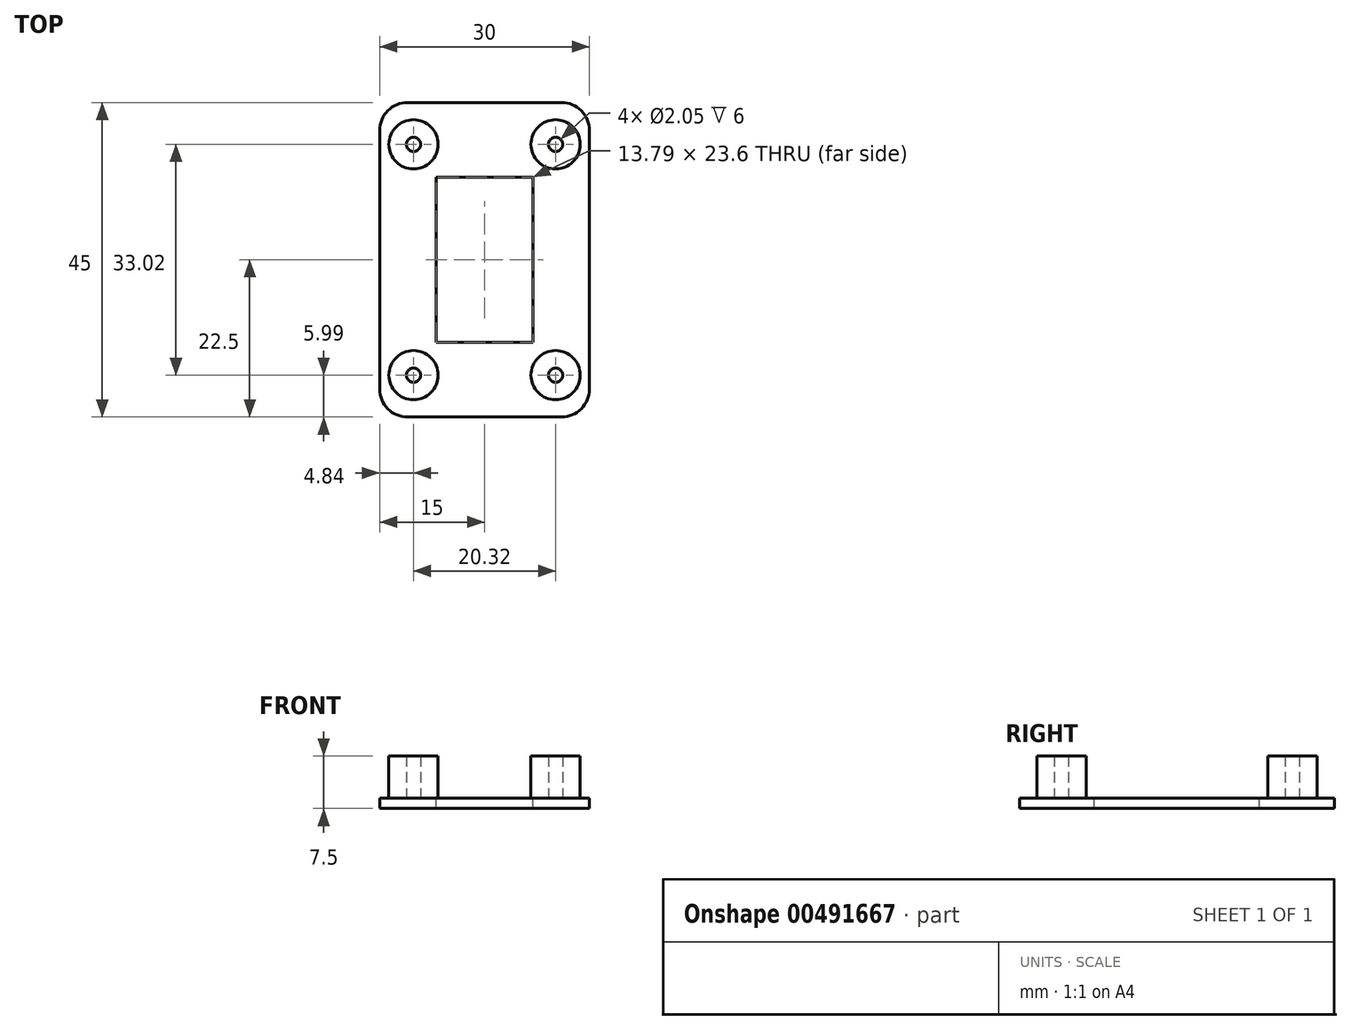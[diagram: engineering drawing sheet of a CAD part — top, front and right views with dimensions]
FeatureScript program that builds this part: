
annotation { "Feature Type Name" : "Feature", "Feature Type Description" : "" }
export const myFeature = defineFeature(function(context is Context, id is Id, definition is map)
    precondition{}
    {
        {
            var Q0;
            Q0=qCreatedBy(makeId("Top.planeOp"),FACE);
            var sketch = newSketch(context, id + "F0", { "sketchPlane" : qUnion([Q0])});
            skLineSegment(sketch, "E0.bottom", {"start": v(-11, 22.5) * mm, "end": v(11, 22.5) * mm});
            skLineSegment(sketch, "E0.top", {"start": v(-11, -22.5) * mm, "end": v(11, -22.5) * mm});
            skLineSegment(sketch, "E0.left", {"start": v(-15, 18.5) * mm, "end": v(-15, -18.5) * mm});
            skLineSegment(sketch, "E0.right", {"start": v(15, 18.5) * mm, "end": v(15, -18.5) * mm});
            skPoint(sketch, "E0.middle", {"position": v(0, 0) * mm});
            skPoint(sketch, "E1.visualSharp", {"position": v(-15, -22.5) * mm});
            skArc(sketch, "E1.filletArc", {"start": v(-15, -18.5) * mm, "mid": v(-13.83, -21.33) * mm, "end": v(-11, -22.5) * mm});
            skPoint(sketch, "E2.visualSharp", {"position": v(15, -22.5) * mm});
            skArc(sketch, "E2.filletArc", {"start": v(11, -22.5) * mm, "mid": v(13.83, -21.33) * mm, "end": v(15, -18.5) * mm});
            skPoint(sketch, "E3.visualSharp", {"position": v(15, 22.5) * mm});
            skArc(sketch, "E3.filletArc", {"start": v(15, 18.5) * mm, "mid": v(13.83, 21.33) * mm, "end": v(11, 22.5) * mm});
            skPoint(sketch, "E4.visualSharp", {"position": v(-15, 22.5) * mm});
            skArc(sketch, "E4.filletArc", {"start": v(-11, 22.5) * mm, "mid": v(-13.83, 21.33) * mm, "end": v(-15, 18.5) * mm});
            skSolve(sketch);
        }
        {
            var Q0;
            Q0=qSketchRegion(id+"F0",true);
            extrude(context, id + "F1", {"entities" : qUnion([Q0]), "depth" : 1.5 * mm});
        }
        {
            var Q0;
            Q0=makeQuery(id+"F1.opExtrude","CAP_FACE",FACE,{"disambiguationData":[OSD([sQuery(id+"F0.wireOp",EDGE,"E0.bottom"),sQuery(id+"F0.wireOp",EDGE,"E0.top"),sQuery(id+"F0.wireOp",EDGE,"E0.left"),sQuery(id+"F0.wireOp",EDGE,"E0.right"),sQuery(id+"F0.wireOp",EDGE,"E1.filletArc"),sQuery(id+"F0.wireOp",EDGE,"E2.filletArc"),sQuery(id+"F0.wireOp",EDGE,"E3.filletArc"),sQuery(id+"F0.wireOp",EDGE,"E4.filletArc")])],"isStart":false});
            var sketch = newSketch(context, id + "F2", { "sketchPlane" : qUnion([Q0])});
            skLineSegment(sketch, "E5.bottom", {"start": v(-10.7, 19.05) * mm, "end": v(10.7, 19.05) * mm, "construction": true});
            skLineSegment(sketch, "E5.top", {"start": v(-10.7, -19.05) * mm, "end": v(10.7, -19.05) * mm, "construction": true});
            skLineSegment(sketch, "E5.left", {"start": v(-12.7, 17.05) * mm, "end": v(-12.7, -17.05) * mm, "construction": true});
            skLineSegment(sketch, "E5.right", {"start": v(12.7, 17.05) * mm, "end": v(12.7, -17.05) * mm, "construction": true});
            skPoint(sketch, "E5.middle", {"position": v(0, 0) * mm});
            skPoint(sketch, "E6.visualSharp", {"position": v(-12.7, -19.05) * mm});
            skArc(sketch, "E6.filletArc", {"start": v(-12.7, -17.05) * mm, "mid": v(-12.11, -18.46) * mm, "end": v(-10.7, -19.05) * mm, "construction": true});
            skPoint(sketch, "E7.visualSharp", {"position": v(12.7, -19.05) * mm});
            skArc(sketch, "E7.filletArc", {"start": v(10.7, -19.05) * mm, "mid": v(12.11, -18.46) * mm, "end": v(12.7, -17.05) * mm, "construction": true});
            skPoint(sketch, "E8.visualSharp", {"position": v(12.7, 19.05) * mm});
            skArc(sketch, "E8.filletArc", {"start": v(12.7, 17.05) * mm, "mid": v(12.11, 18.46) * mm, "end": v(10.7, 19.05) * mm, "construction": true});
            skPoint(sketch, "E9.visualSharp", {"position": v(-12.7, 19.05) * mm});
            skArc(sketch, "E9.filletArc", {"start": v(-10.7, 19.05) * mm, "mid": v(-12.11, 18.46) * mm, "end": v(-12.7, 17.05) * mm, "construction": true});
            skCircle(sketch, "E10", {"center": v(-10.16, 16.5) * mm, "radius": 1.02 * mm});
            skCircle(sketch, "E11", {"center": v(-10.16, 16.5) * mm, "radius": 3.52 * mm});
            skLineSegment(sketch, "E12", {"start": v(0, 19.05) * mm, "end": v(0, -19.05) * mm, "construction": true});
            skLineSegment(sketch, "E13", {"start": v(-12.7, 0) * mm, "end": v(12.7, 0) * mm, "construction": true});
            skCircle(sketch, "E14.MirrorC", {"center": v(10.16, 16.5) * mm, "radius": 3.52 * mm});
            skCircle(sketch, "E15.MirrorC", {"center": v(10.16, 16.5) * mm, "radius": 1.02 * mm});
            skCircle(sketch, "E16.MirrorC", {"center": v(-10.16, -16.51) * mm, "radius": 1.02 * mm});
            skCircle(sketch, "E17.MirrorC", {"center": v(-10.16, -16.51) * mm, "radius": 3.52 * mm});
            skCircle(sketch, "E18.MirrorC", {"center": v(10.16, -16.5) * mm, "radius": 1.02 * mm});
            skCircle(sketch, "E19.MirrorC", {"center": v(10.16, -16.5) * mm, "radius": 3.52 * mm});
            skSolve(sketch);
        }
        {
            var Q0;
            Q0=qSketchRegion(id+"F2",true);
            extrude(context, id + "F3", {"entities" : qUnion([Q0]), "operationType" : NewBodyOperationType.ADD, "depth" : 6 * mm, "offsetDistance" : 25 * mm});
        }
        {
            var Q0;
            {var subQ0=sQuery(id+"F0.wireOp",EDGE,"E4.filletArc");var subQ1=sQuery(id+"F0.wireOp",EDGE,"E3.filletArc");var subQ2=sQuery(id+"F0.wireOp",EDGE,"E2.filletArc");var subQ3=sQuery(id+"F0.wireOp",EDGE,"E1.filletArc");var subQ4=sQuery(id+"F0.wireOp",EDGE,"E0.bottom");var subQ5=sQuery(id+"F0.wireOp",EDGE,"E0.right");var subQ6=sQuery(id+"F0.wireOp",EDGE,"E0.top");var subQ7=sQuery(id+"F0.wireOp",EDGE,"E0.left");Q0=makeQuery(id+"F3.boolean.opBoolean","SPLIT",FACE,{"disambiguationData":[TD([makeQuery(id+"F1.opExtrude","SWEPT_FACE",FACE,{"disambiguationData":[OSD([subQ4])]})])],"derivedFrom":makeQuery(id+"F1.opExtrude","CAP_FACE",FACE,{"disambiguationData":[OSD([subQ4,subQ6,subQ7,subQ5,subQ3,subQ2,subQ1,subQ0])],"isStart":false})});}
            var sketch = newSketch(context, id + "F4", { "sketchPlane" : qUnion([Q0])});
            skLineSegment(sketch, "E20.bottom", {"start": v(-6.9, 11.8) * mm, "end": v(6.9, 11.8) * mm});
            skLineSegment(sketch, "E20.top", {"start": v(-6.9, -11.8) * mm, "end": v(6.9, -11.8) * mm});
            skLineSegment(sketch, "E20.left", {"start": v(-6.9, 11.8) * mm, "end": v(-6.9, -11.8) * mm});
            skLineSegment(sketch, "E20.right", {"start": v(6.9, 11.8) * mm, "end": v(6.9, -11.8) * mm});
            skPoint(sketch, "E20.middle", {"position": v(0, 0) * mm});
            skSolve(sketch);
        }
        {
            var Q0;
            Q0 = qSketchRegion(id + "F4", true);
            extrude(context, id + "F5", {"entities" : qUnion([Q0]), "operationType" : NewBodyOperationType.REMOVE, "oppositeDirection" : true, "depth" : 2 * mm});
        }
    });
